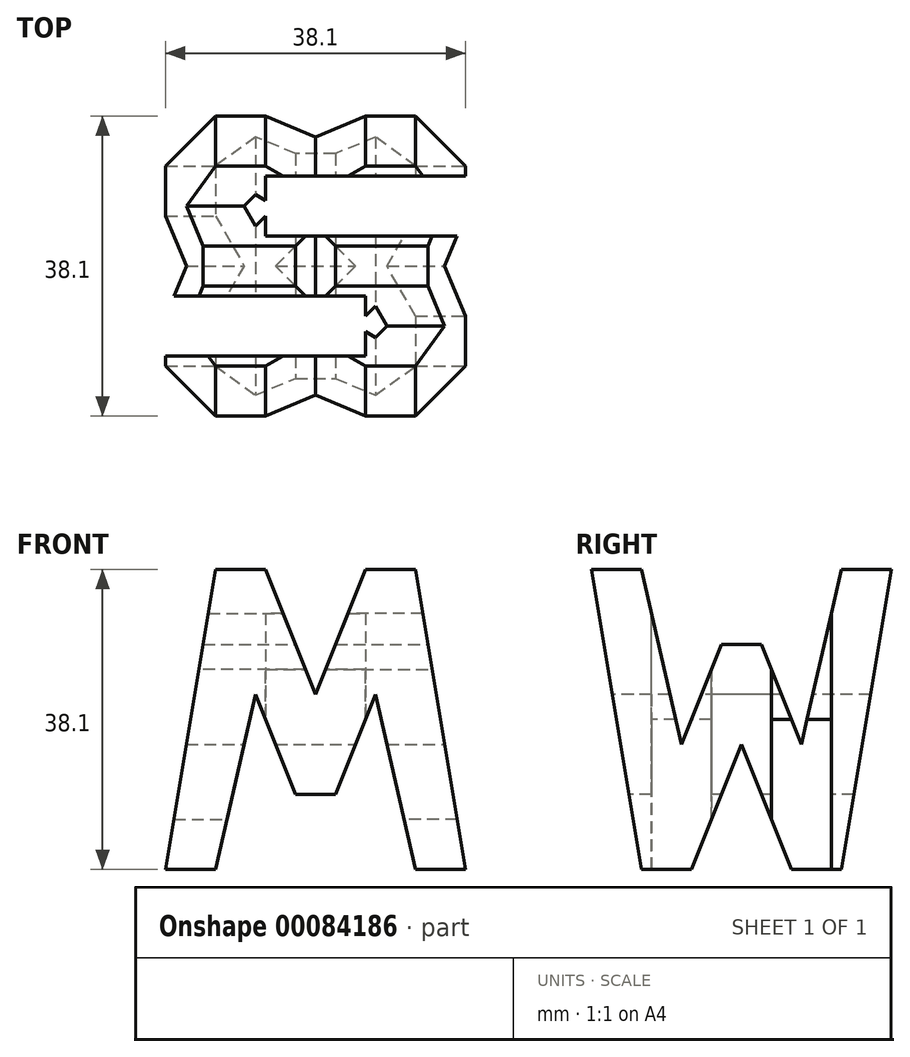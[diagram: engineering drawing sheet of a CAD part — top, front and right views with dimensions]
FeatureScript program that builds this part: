
annotation { "Feature Type Name" : "Feature", "Feature Type Description" : "" }
export const myFeature = defineFeature(function(context is Context, id is Id, definition is map)
    precondition{}
    {
        {
            var Q0;
            Q0=qCreatedBy(makeId("Front.planeOp"),FACE);
            var sketch = newSketch(context, id + "F0", { "sketchPlane" : qUnion([Q0])});
            skLineSegment(sketch, "E0", {"start": v(0, 0) * mm, "end": v(0, 38.1) * mm});
            skLineSegment(sketch, "E1", {"start": v(0, 38.1) * mm, "end": v(38.1, 38.1) * mm});
            skLineSegment(sketch, "E2", {"start": v(38.1, 38.1) * mm, "end": v(38.1, 0) * mm});
            skLineSegment(sketch, "E3", {"start": v(38.1, 0) * mm, "end": v(0, 0) * mm});
            skSolve(sketch);
        }
        {
            var Q0;
            Q0=makeQuery(id+"F0.imprint","IMPRINT",FACE,{"disambiguationData":[TD([[makeQuery(id+"F0.imprint","IMPRINT",EDGE,{"derivedFrom":sQuery(id+"F0.wireOp",EDGE,"E0")}),-1.0]])]});
            extrude(context, id + "F1", {"entities" : qUnion([Q0]), "depth" : 38.1 * mm});
        }
        {
            var Q0;
            Q0=qCreatedBy(makeId("Front.planeOp"),FACE);
            cPlane(context, id + "F2", {"entities" : qUnion([Q0]), "cplaneType" : CPlaneType.OFFSET, "offset" : 38.1 * mm, "width" : 152.4 * mm, "height" : 152.4 * mm});
        }
        {
            var Q0;
            Q0=qCreatedBy(makeId("Top.planeOp"),FACE);
            cPlane(context, id + "F3", {"entities" : qUnion([Q0]), "cplaneType" : CPlaneType.OFFSET, "offset" : 38.1 * mm, "width" : 152.4 * mm, "height" : 152.4 * mm});
        }
        {
            var Q0;
            Q0=makeQuery(id+"F1.opExtrude","SWEPT_FACE",FACE,{"disambiguationData":[OSD([sQuery(id+"F0.wireOp",EDGE,"E2")])]});
            var sketch = newSketch(context, id + "F4", { "sketchPlane" : qUnion([Q0])});
            skLineSegment(sketch, "E4", {"start": v(-38.1, 38.1) * mm, "end": v(-31.75, 0) * mm});
            skLineSegment(sketch, "E5", {"start": v(-31.75, 0) * mm, "end": v(-25.4, 0) * mm});
            skLineSegment(sketch, "E6", {"start": v(-25.4, 0) * mm, "end": v(-19.05, 15.88) * mm});
            skLineSegment(sketch, "E7", {"start": v(-19.05, 15.88) * mm, "end": v(-12.7, 0) * mm});
            skLineSegment(sketch, "E8", {"start": v(-12.7, 0) * mm, "end": v(-6.35, 0) * mm});
            skLineSegment(sketch, "E9", {"start": v(-6.35, 0) * mm, "end": v(0, 38.1) * mm});
            skLineSegment(sketch, "E10", {"start": v(0, 38.1) * mm, "end": v(-6.35, 38.1) * mm});
            skLineSegment(sketch, "E11", {"start": v(-6.35, 38.1) * mm, "end": v(-11.43, 15.88) * mm});
            skLineSegment(sketch, "E12", {"start": v(-11.43, 15.88) * mm, "end": v(-16.51, 28.58) * mm});
            skLineSegment(sketch, "E13", {"start": v(-16.51, 28.58) * mm, "end": v(-21.59, 28.58) * mm});
            skLineSegment(sketch, "E14", {"start": v(-21.59, 28.58) * mm, "end": v(-26.67, 15.88) * mm});
            skLineSegment(sketch, "E15", {"start": v(-26.67, 15.88) * mm, "end": v(-31.75, 38.1) * mm});
            skLineSegment(sketch, "E16", {"start": v(-31.75, 38.1) * mm, "end": v(-38.1, 38.1) * mm});
            skSolve(sketch);
        }
        {
            var Q0;
            {var subQ0=sQuery(id+"F4.wireOp",EDGE,"E11");Q0=makeQuery(id+"F4.imprint","IMPRINT",FACE,{"disambiguationData":[TD([[makeQuery(id+"F4.imprint","IMPRINT",EDGE,{"derivedFrom":subQ0}),-1.0]])]});}
            var Q1;
            {var subQ0=sQuery(id+"F4.wireOp",EDGE,"E9");Q1=makeQuery(id+"F4.imprint","IMPRINT",FACE,{"disambiguationData":[TD([[makeQuery(id+"F4.imprint","IMPRINT",EDGE,{"derivedFrom":subQ0}),-1.0]])]});}
            var Q2;
            {var subQ0=sQuery(id+"F4.wireOp",EDGE,"E6");Q2=makeQuery(id+"F4.imprint","IMPRINT",FACE,{"disambiguationData":[TD([[makeQuery(id+"F4.imprint","IMPRINT",EDGE,{"derivedFrom":subQ0}),-1.0]])]});}
            var Q3;
            {var subQ0=sQuery(id+"F4.wireOp",EDGE,"E4");Q3=makeQuery(id+"F4.imprint","IMPRINT",FACE,{"disambiguationData":[TD([[makeQuery(id+"F4.imprint","IMPRINT",EDGE,{"derivedFrom":subQ0}),-1.0]])]});}
            extrude(context, id + "F5", {"entities" : qUnion([Q0, Q1, Q2, Q3]), "operationType" : NewBodyOperationType.REMOVE, "oppositeDirection" : true, "depth" : 38.1 * mm});
        }
        {
            var Q0;
            Q0=qCreatedBy(id+"F2.planeOp",FACE);
            var sketch = newSketch(context, id + "F6", { "sketchPlane" : qUnion([Q0])});
            skLineSegment(sketch, "E17", {"start": v(0, 0) * mm, "end": v(0, 38.1) * mm});
            skLineSegment(sketch, "E18", {"start": v(0, 38.1) * mm, "end": v(38.1, 38.1) * mm});
            skLineSegment(sketch, "E19", {"start": v(38.1, 38.1) * mm, "end": v(38.1, 0) * mm});
            skLineSegment(sketch, "E20", {"start": v(38.1, 0) * mm, "end": v(0, 0) * mm});
            skLineSegment(sketch, "E21", {"start": v(38.1, 0) * mm, "end": v(31.75, 38.1) * mm});
            skLineSegment(sketch, "E22", {"start": v(31.75, 38.1) * mm, "end": v(25.4, 38.1) * mm});
            skLineSegment(sketch, "E23", {"start": v(25.4, 38.1) * mm, "end": v(19.05, 22.22) * mm});
            skLineSegment(sketch, "E24", {"start": v(19.05, 22.22) * mm, "end": v(12.7, 38.1) * mm});
            skLineSegment(sketch, "E25", {"start": v(12.7, 38.1) * mm, "end": v(6.35, 38.1) * mm});
            skLineSegment(sketch, "E26", {"start": v(6.35, 38.1) * mm, "end": v(0, 0) * mm});
            skLineSegment(sketch, "E27", {"start": v(6.35, 0) * mm, "end": v(11.43, 22.22) * mm});
            skLineSegment(sketch, "E28", {"start": v(11.43, 22.22) * mm, "end": v(16.5, 9.52) * mm});
            skLineSegment(sketch, "E29", {"start": v(16.5, 9.53) * mm, "end": v(21.59, 9.53) * mm});
            skLineSegment(sketch, "E30", {"start": v(21.59, 9.53) * mm, "end": v(26.67, 22.23) * mm});
            skLineSegment(sketch, "E31", {"start": v(26.67, 22.23) * mm, "end": v(31.75, 0) * mm});
            skLineSegment(sketch, "E32", {"start": v(31.75, 0) * mm, "end": v(38.1, 0) * mm});
            skSolve(sketch);
        }
        {
            var Q0;
            {var subQ0=sQuery(id+"F6.wireOp",EDGE,"E17");Q0=makeQuery(id+"F6.imprint","IMPRINT",FACE,{"disambiguationData":[TD([[makeQuery(id+"F6.imprint","IMPRINT",EDGE,{"derivedFrom":subQ0}),-1.0]])]});}
            var Q1;
            {var subQ0=sQuery(id+"F6.wireOp",EDGE,"E23");Q1=makeQuery(id+"F6.imprint","IMPRINT",FACE,{"disambiguationData":[TD([[makeQuery(id+"F6.imprint","IMPRINT",EDGE,{"derivedFrom":subQ0}),-1.0]])]});}
            var Q2;
            {var subQ0=sQuery(id+"F6.wireOp",EDGE,"E19");Q2=makeQuery(id+"F6.imprint","IMPRINT",FACE,{"disambiguationData":[TD([[makeQuery(id+"F6.imprint","IMPRINT",EDGE,{"derivedFrom":subQ0}),-1.0]])]});}
            var Q3;
            {var subQ0=sQuery(id+"F6.wireOp",EDGE,"E27");Q3=makeQuery(id+"F6.imprint","IMPRINT",FACE,{"disambiguationData":[TD([[makeQuery(id+"F6.imprint","IMPRINT",EDGE,{"derivedFrom":subQ0}),-1.0]])]});}
            extrude(context, id + "F7", {"entities" : qUnion([Q0, Q1, Q2, Q3]), "operationType" : NewBodyOperationType.REMOVE, "oppositeDirection" : true, "depth" : 38.1 * mm});
        }
        {
            var Q0;
            Q0=qCreatedBy(id+"F3.planeOp",FACE);
            var sketch = newSketch(context, id + "F8", { "sketchPlane" : qUnion([Q0])});
            skLineSegment(sketch, "E33", {"start": v(0, 0) * mm, "end": v(0, -38.1) * mm});
            skLineSegment(sketch, "E34", {"start": v(0, -38.1) * mm, "end": v(38.1, -38.1) * mm});
            skLineSegment(sketch, "E35", {"start": v(38.1, -38.1) * mm, "end": v(38.1, 0) * mm});
            skLineSegment(sketch, "E36", {"start": v(38.1, 0) * mm, "end": v(0, 0) * mm});
            skLineSegment(sketch, "E37", {"start": v(38.1, -7.62) * mm, "end": v(12.7, -7.62) * mm});
            skLineSegment(sketch, "E38", {"start": v(12.7, -7.62) * mm, "end": v(12.7, -15.24) * mm});
            skLineSegment(sketch, "E39", {"start": v(12.7, -15.24) * mm, "end": v(38.1, -15.24) * mm});
            skLineSegment(sketch, "E40", {"start": v(0, -30.48) * mm, "end": v(25.4, -30.48) * mm});
            skLineSegment(sketch, "E41", {"start": v(25.4, -30.48) * mm, "end": v(25.4, -22.86) * mm});
            skLineSegment(sketch, "E42", {"start": v(25.4, -22.86) * mm, "end": v(0, -22.86) * mm});
            skSolve(sketch);
        }
        {
            var Q0;
            {var subQ0=sQuery(id+"F8.wireOp",EDGE,"E37");Q0=makeQuery(id+"F8.imprint","IMPRINT",FACE,{"disambiguationData":[TD([[makeQuery(id+"F8.imprint","IMPRINT",EDGE,{"derivedFrom":subQ0}),1.0]])]});}
            var Q1;
            {var subQ0=sQuery(id+"F8.wireOp",EDGE,"E40");Q1=makeQuery(id+"F8.imprint","IMPRINT",FACE,{"disambiguationData":[TD([[makeQuery(id+"F8.imprint","IMPRINT",EDGE,{"derivedFrom":subQ0}),1.0]])]});}
            extrude(context, id + "F9", {"entities" : qUnion([Q0, Q1]), "operationType" : NewBodyOperationType.REMOVE, "oppositeDirection" : true, "depth" : 38.1 * mm});
        }
    });
